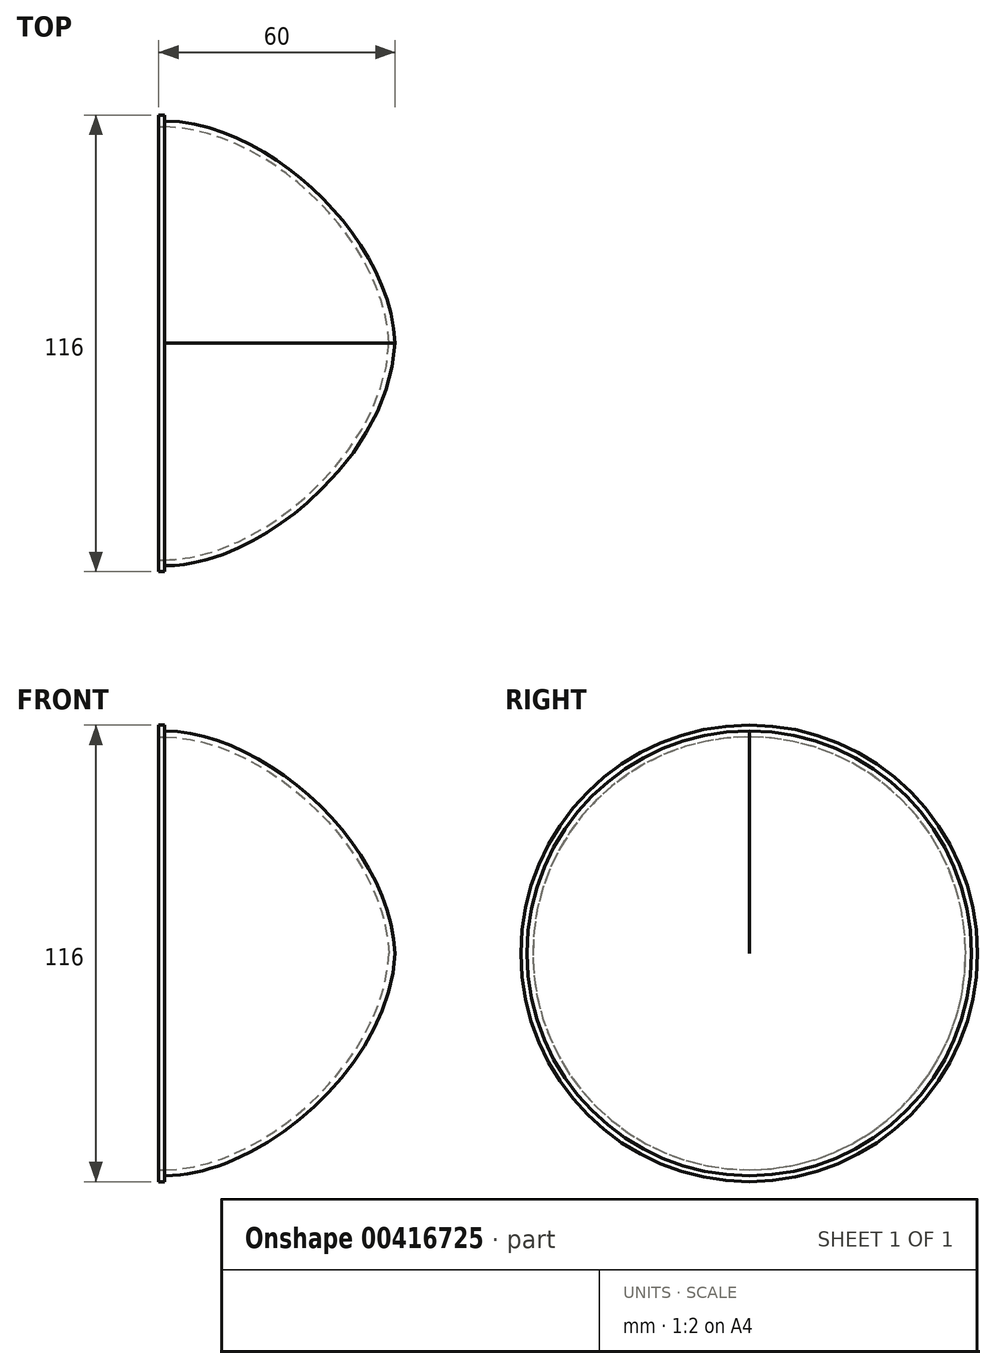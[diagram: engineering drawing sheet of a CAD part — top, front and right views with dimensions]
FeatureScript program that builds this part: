
annotation { "Feature Type Name" : "Feature", "Feature Type Description" : "" }
export const myFeature = defineFeature(function(context is Context, id is Id, definition is map)
    precondition{}
    {
        {
            var Q0;
            Q0=qCreatedBy(makeId("Front.planeOp"),FACE);
            var sketch = newSketch(context, id + "F0", { "sketchPlane" : qUnion([Q0])});
            skLineSegment(sketch, "E0", {"start": v(0, 55) * mm, "end": v(0, 58) * mm});
            skLineSegment(sketch, "E1", {"start": v(0, 58) * mm, "end": v(1.5, 58) * mm});
            skLineSegment(sketch, "E2", {"start": v(1.5, 58) * mm, "end": v(1.5, 56.5) * mm});
            skLineSegment(sketch, "E3", {"start": v(0, 55) * mm, "end": v(1.5, 55) * mm});
            skFitSpline(sketch, "E4", {"points": [v(1.5, 55) * mm, v(58.5, 0) * mm, v(1.5, -55) * mm], "startDerivative": vector(148.9, -1.06) * mm, "endDerivative": vector(-180.24, -0.8) * mm});
            skFitSpline(sketch, "E5", {"points": [v(1.5, 56.5) * mm, v(60, 0) * mm, v(1.5, -56.5) * mm], "startDerivative": vector(148.9, -0.17) * mm, "endDerivative": vector(-180.24, -0.2) * mm});
            skLineSegment(sketch, "E6", {"start": v(58.5, 0) * mm, "end": v(60, 0) * mm});
            skPoint(sketch, "E7.start.orphan", {"position": v(-7.13, 0) * mm});
            skLineSegment(sketch, "E8", {"start": v(60, 0) * mm, "end": v(0, 0) * mm});
            skSolve(sketch);
        }
        {
            var Q0;
            Q0=makeQuery(id+"F0.imprint","IMPRINT",FACE,{"disambiguationData":[TD([[makeQuery(id+"F0.imprint","IMPRINT",EDGE,{"derivedFrom":sQuery(id+"F0.wireOp",EDGE,"E0")}),-1.0]])]});
            var Q1;
            Q1=sQuery(id+"F0.wireOp",EDGE,"E8");
            revolve(context, id + "F1", {"entities" : qUnion([Q0]), "axis" : qUnion([Q1]), "revolveType" : RevolveType.FULL});
        }
    });
